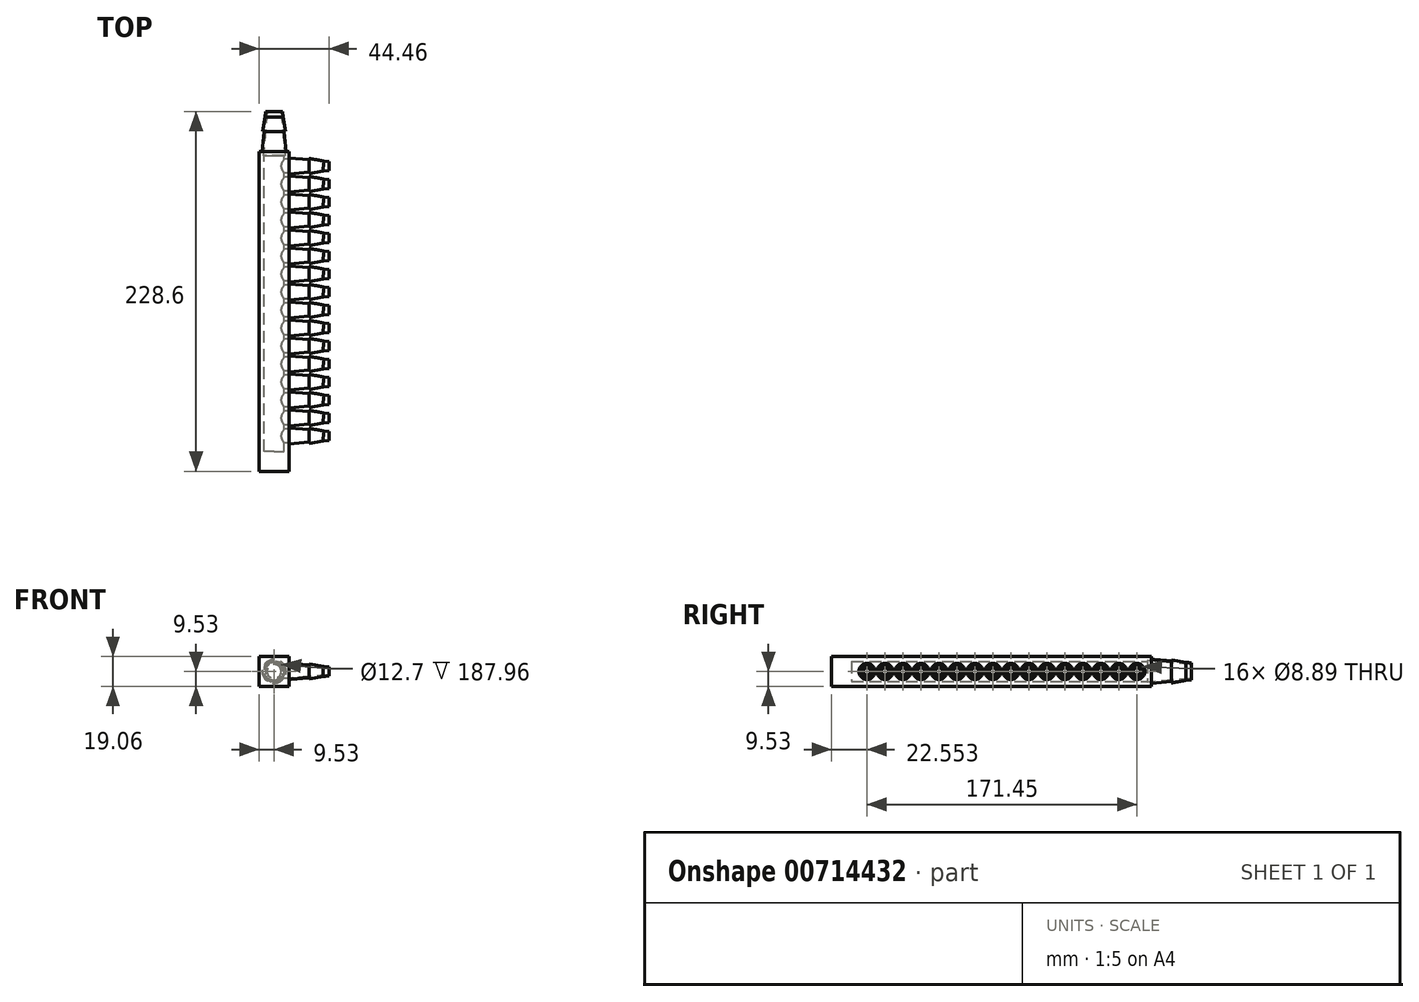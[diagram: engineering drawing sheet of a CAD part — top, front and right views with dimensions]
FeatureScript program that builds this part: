
annotation { "Feature Type Name" : "Feature", "Feature Type Description" : "" }
export const myFeature = defineFeature(function(context is Context, id is Id, definition is map)
    precondition{}
    {
        {
            var Q0;
            Q0=qCreatedBy(makeId("Front.planeOp"),FACE);
            var sketch = newSketch(context, id + "F0", { "sketchPlane" : qUnion([Q0])});
            skCircle(sketch, "E0", {"center": v(0, 0) * mm, "radius": 6.35 * mm});
            skSolve(sketch);
        }
        {
            var Q0;
            Q0=qCreatedBy(makeId("Front.planeOp"),FACE);
            var sketch = newSketch(context, id + "F1", { "sketchPlane" : qUnion([Q0])});
            skLineSegment(sketch, "E1.bottom", {"start": v(9.53, 9.52) * mm, "end": v(-9.53, 9.52) * mm});
            skLineSegment(sketch, "E1.top", {"start": v(9.53, -9.53) * mm, "end": v(-9.53, -9.53) * mm});
            skLineSegment(sketch, "E1.left", {"start": v(9.53, 9.52) * mm, "end": v(9.53, -9.53) * mm});
            skLineSegment(sketch, "E1.right", {"start": v(-9.53, 9.52) * mm, "end": v(-9.53, -9.53) * mm});
            skPoint(sketch, "E1.middle", {"position": v(0, 0) * mm});
            skSolve(sketch);
        }
        {
            var Q0;
            Q0 = qSketchRegion(id + "F1", true);
            extrude(context, id + "F2", {"entities" : qUnion([Q0]), "depth" : 203.2 * mm, "offsetDistance" : 25.4 * mm});
        }
        {
            var Q0;
            Q0 = qSketchRegion(id + "F0", true);
            extrude(context, id + "F3", {"entities" : qUnion([Q0]), "operationType" : NewBodyOperationType.REMOVE, "depth" : 190.5 * mm, "offsetDistance" : 25.4 * mm, "hasSecondDirectionDraft" : true, "secondDirectionDraftAngle" : 5 * degree, "secondDirectionDraftPullDirection" : true});
        }
        {
            var Q0;
            Q0=makeQuery(id+"F2.opExtrude","SWEPT_FACE",FACE,{"disambiguationData":[OSD([sQuery(id+"F1.wireOp",EDGE,"E1.left")])]});
            var sketch = newSketch(context, id + "F4", { "sketchPlane" : qUnion([Q0])});
            skCircle(sketch, "E2", {"center": v(-9.23, 0) * mm, "radius": 5.08 * mm});
            skCircle(sketch, "E3.1.0.0", {"center": v(-20.66, 0) * mm, "radius": 5.08 * mm});
            skCircle(sketch, "E3.2.0.0", {"center": v(-32.09, 0) * mm, "radius": 5.08 * mm});
            skCircle(sketch, "E3.3.0.0", {"center": v(-43.52, 0) * mm, "radius": 5.08 * mm});
            skCircle(sketch, "E3.4.0.0", {"center": v(-54.95, 0) * mm, "radius": 5.08 * mm});
            skCircle(sketch, "E3.5.0.0", {"center": v(-66.38, 0) * mm, "radius": 5.08 * mm});
            skCircle(sketch, "E3.6.0.0", {"center": v(-77.8, 0) * mm, "radius": 5.08 * mm});
            skCircle(sketch, "E3.7.0.0", {"center": v(-89.24, 0) * mm, "radius": 5.08 * mm});
            skCircle(sketch, "E3.8.0.0", {"center": v(-100.67, 0) * mm, "radius": 5.08 * mm});
            skCircle(sketch, "E3.9.0.0", {"center": v(-112.1, 0) * mm, "radius": 5.08 * mm});
            skCircle(sketch, "E3.10.0.0", {"center": v(-123.53, 0) * mm, "radius": 5.08 * mm});
            skCircle(sketch, "E3.11.0.0", {"center": v(-134.96, 0) * mm, "radius": 5.08 * mm});
            skCircle(sketch, "E3.12.0.0", {"center": v(-146.39, 0) * mm, "radius": 5.08 * mm});
            skCircle(sketch, "E3.13.0.0", {"center": v(-157.82, 0) * mm, "radius": 5.08 * mm});
            skCircle(sketch, "E3.14.0.0", {"center": v(-169.25, 0) * mm, "radius": 5.08 * mm});
            skCircle(sketch, "E3.15.0.0", {"center": v(-180.68, 0) * mm, "radius": 5.08 * mm});
            skLineSegment(sketch, "E3.direction1", {"start": v(-9.23, 0) * mm, "end": v(-20.66, 0) * mm, "construction": true});
            skSolve(sketch);
        }
        {
            var Q0;
            Q0=makeQuery(id+"F4.imprint","IMPRINT",FACE,{"disambiguationData":[TD([[makeQuery(id+"F4.imprint","IMPRINT",EDGE,{"derivedFrom":sQuery(id+"F4.wireOp",EDGE,"E2")}),-1.0]])]});
            var sketch = newSketch(context, id + "F5", { "sketchPlane" : qUnion([Q0])});
            skCircle(sketch, "E4", {"center": v(-9.2, 0) * mm, "radius": 4.45 * mm});
            skCircle(sketch, "E5.1.0.0", {"center": v(-20.63, 0) * mm, "radius": 4.45 * mm});
            skCircle(sketch, "E5.2.0.0", {"center": v(-32.06, 0) * mm, "radius": 4.45 * mm});
            skCircle(sketch, "E5.3.0.0", {"center": v(-43.49, 0) * mm, "radius": 4.45 * mm});
            skCircle(sketch, "E5.4.0.0", {"center": v(-54.92, 0) * mm, "radius": 4.45 * mm});
            skCircle(sketch, "E5.5.0.0", {"center": v(-66.35, 0) * mm, "radius": 4.45 * mm});
            skCircle(sketch, "E5.6.0.0", {"center": v(-77.78, 0) * mm, "radius": 4.45 * mm});
            skCircle(sketch, "E5.7.0.0", {"center": v(-89.2, 0) * mm, "radius": 4.45 * mm});
            skCircle(sketch, "E5.8.0.0", {"center": v(-100.64, 0) * mm, "radius": 4.45 * mm});
            skCircle(sketch, "E5.9.0.0", {"center": v(-112.07, 0) * mm, "radius": 4.45 * mm});
            skCircle(sketch, "E5.10.0.0", {"center": v(-123.5, 0) * mm, "radius": 4.45 * mm});
            skCircle(sketch, "E5.11.0.0", {"center": v(-134.93, 0) * mm, "radius": 4.45 * mm});
            skCircle(sketch, "E5.12.0.0", {"center": v(-146.36, 0) * mm, "radius": 4.45 * mm});
            skCircle(sketch, "E5.13.0.0", {"center": v(-157.79, 0) * mm, "radius": 4.45 * mm});
            skCircle(sketch, "E5.14.0.0", {"center": v(-169.22, 0) * mm, "radius": 4.45 * mm});
            skCircle(sketch, "E5.15.0.0", {"center": v(-180.65, 0) * mm, "radius": 4.45 * mm});
            skLineSegment(sketch, "E5.direction1", {"start": v(-9.2, 0) * mm, "end": v(-20.63, 0) * mm, "construction": true});
            skSolve(sketch);
        }
        {
            var Q0;
            Q0 = qSketchRegion(id + "F4", true);
            extrude(context, id + "F6", {"entities" : qUnion([Q0]), "operationType" : NewBodyOperationType.ADD, "depth" : 25.4 * mm, "offsetDistance" : 25.4 * mm, "hasDraft" : true, "draftAngle" : 5 * degree, "draftPullDirection" : true});
        }
        {
            var Q0;
            Q0=makeQuery(id+"F2.opExtrude","CAP_FACE",FACE,{"disambiguationData":[OSD([sQuery(id+"F1.wireOp",EDGE,"E1.bottom"),sQuery(id+"F1.wireOp",EDGE,"E1.top"),sQuery(id+"F1.wireOp",EDGE,"E1.left"),sQuery(id+"F1.wireOp",EDGE,"E1.right")])],"isStart":true});
            var sketch = newSketch(context, id + "F7", { "sketchPlane" : qUnion([Q0])});
            skCircle(sketch, "E6", {"center": v(0, 0) * mm, "radius": 7.62 * mm});
            skSolve(sketch);
        }
        {
            var Q0;
            Q0 = qSketchRegion(id + "F7", true);
            extrude(context, id + "F8", {"entities" : qUnion([Q0]), "operationType" : NewBodyOperationType.ADD, "depth" : 25.4 * mm, "offsetDistance" : 25.4 * mm, "hasDraft" : true, "draftAngle" : 5 * degree, "draftPullDirection" : true});
        }
        {
            var Q0;
            Q0=makeQuery(id+"F8.opExtrude","CAP_FACE",FACE,{"disambiguationData":[OSD([sQuery(id+"F7.wireOp",EDGE,"E6")])],"isStart":false});
            var sketch = newSketch(context, id + "F9", { "sketchPlane" : qUnion([Q0])});
            skCircle(sketch, "E7", {"center": v(0, 0) * mm, "radius": 4.45 * mm});
            skSolve(sketch);
        }
        {
            var Q0;
            Q0=makeQuery(id+"F8.opExtrude","CAP_FACE",FACE,{"disambiguationData":[OSD([sQuery(id+"F7.wireOp",EDGE,"E6")])],"isStart":false});
            var sketch = newSketch(context, id + "F10", { "sketchPlane" : qUnion([Q0])});
            skCircle(sketch, "E8", {"center": v(0, 0) * mm, "radius": 5.08 * mm});
            skSolve(sketch);
        }
        {
            var Q0;
            Q0 = qSketchRegion(id + "F10", true);
            extrude(context, id + "F11", {"entities" : qUnion([Q0]), "operationType" : NewBodyOperationType.ADD, "oppositeDirection" : true, "depth" : 12.7 * mm, "offsetDistance" : 25.4 * mm, "hasDraft" : true, "draftAngle" : 10 * degree});
        }
        {
            var Q0;
            Q0=makeQuery(id+"F9.imprint","IMPRINT",FACE,{"disambiguationData":[TD([[makeQuery(id+"F9.imprint","IMPRINT",EDGE,{"derivedFrom":sQuery(id+"F9.wireOp",EDGE,"E7")}),1.0]])]});
            extrude(context, id + "F12", {"entities" : qUnion([Q0]), "operationType" : NewBodyOperationType.REMOVE, "oppositeDirection" : true, "depth" : 27.94 * mm, "offsetDistance" : 25.4 * mm, "hasDraft" : true, "draftAngle" : 5 * degree});
        }
        {
            var Q0;
            Q0=makeQuery(id+"F6.opExtrude","CAP_FACE",FACE,{"disambiguationData":[OSD([sQuery(id+"F4.wireOp",EDGE,"E2")])],"isStart":false});
            var sketch = newSketch(context, id + "F13", { "sketchPlane" : qUnion([Q0])});
            skCircle(sketch, "E9", {"center": v(-9.2, 0) * mm, "radius": 2.54 * mm});
            skCircle(sketch, "E10.1.0.0", {"center": v(-20.63, 0) * mm, "radius": 2.54 * mm});
            skCircle(sketch, "E10.2.0.0", {"center": v(-32.06, 0) * mm, "radius": 2.54 * mm});
            skCircle(sketch, "E10.3.0.0", {"center": v(-43.49, 0) * mm, "radius": 2.54 * mm});
            skCircle(sketch, "E10.4.0.0", {"center": v(-54.92, 0) * mm, "radius": 2.54 * mm});
            skCircle(sketch, "E10.5.0.0", {"center": v(-66.35, 0) * mm, "radius": 2.54 * mm});
            skCircle(sketch, "E10.6.0.0", {"center": v(-77.78, 0) * mm, "radius": 2.54 * mm});
            skCircle(sketch, "E10.7.0.0", {"center": v(-89.2, 0) * mm, "radius": 2.54 * mm});
            skCircle(sketch, "E10.8.0.0", {"center": v(-100.64, 0) * mm, "radius": 2.54 * mm});
            skCircle(sketch, "E10.9.0.0", {"center": v(-112.07, 0) * mm, "radius": 2.54 * mm});
            skCircle(sketch, "E10.10.0.0", {"center": v(-123.5, 0) * mm, "radius": 2.54 * mm});
            skCircle(sketch, "E10.11.0.0", {"center": v(-134.93, 0) * mm, "radius": 2.54 * mm});
            skCircle(sketch, "E10.12.0.0", {"center": v(-146.36, 0) * mm, "radius": 2.54 * mm});
            skCircle(sketch, "E10.13.0.0", {"center": v(-157.79, 0) * mm, "radius": 2.54 * mm});
            skCircle(sketch, "E10.14.0.0", {"center": v(-169.22, 0) * mm, "radius": 2.54 * mm});
            skCircle(sketch, "E10.15.0.0", {"center": v(-180.65, 0) * mm, "radius": 2.54 * mm});
            skLineSegment(sketch, "E10.direction1", {"start": v(-9.2, 0) * mm, "end": v(-20.63, 0) * mm, "construction": true});
            skSolve(sketch);
        }
        {
            var Q0;
            Q0 = qSketchRegion(id + "F13", true);
            extrude(context, id + "F14", {"entities" : qUnion([Q0]), "operationType" : NewBodyOperationType.ADD, "oppositeDirection" : true, "depth" : 12.7 * mm, "offsetDistance" : 25.4 * mm, "hasDraft" : true, "draftAngle" : 10 * degree});
        }
        {
            var Q0;
            Q0 = qSketchRegion(id + "F5", true);
            extrude(context, id + "F15", {"entities" : qUnion([Q0]), "operationType" : NewBodyOperationType.REMOVE, "depth" : 25.4 * mm, "offsetDistance" : 25.4 * mm, "hasDraft" : true, "draftAngle" : 5 * degree, "draftPullDirection" : true, "hasSecondDirection" : true, "secondDirectionOppositeDirection" : true, "secondDirectionDepth" : 12.7 * mm});
        }
    });
